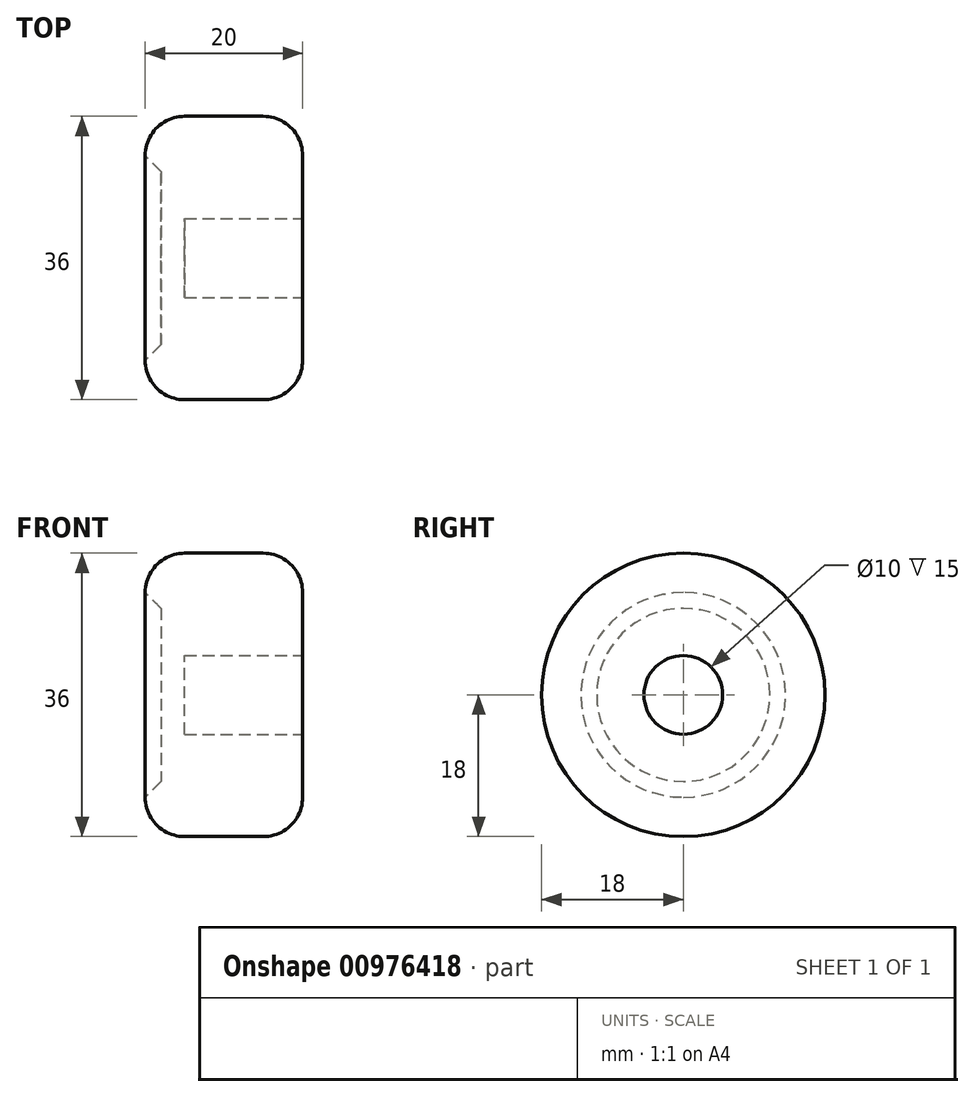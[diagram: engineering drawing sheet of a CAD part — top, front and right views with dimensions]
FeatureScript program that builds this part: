
annotation { "Feature Type Name" : "Feature", "Feature Type Description" : "" }
export const myFeature = defineFeature(function(context is Context, id is Id, definition is map)
    precondition{}
    {
        {
            var Q0;
            Q0=qCreatedBy(makeId("Right.planeOp"),FACE);
            var sketch = newSketch(context, id + "F0", { "sketchPlane" : qUnion([Q0])});
            skCircle(sketch, "E0", {"center": v(0, 0) * mm, "radius": 18 * mm});
            skSolve(sketch);
        }
        {
            var Q0;
            Q0 = qSketchRegion(id + "F0", true);
            extrude(context, id + "F1", {"entities" : qUnion([Q0]), "depth" : 20 * mm, "offsetDistance" : 25 * mm});
        }
        {
            var Q0;
            Q0=makeQuery(id+"F1.opExtrude","CAP_FACE",FACE,{"disambiguationData":[OSD([sQuery(id+"F0.wireOp",EDGE,"E0")])],"isStart":false});
            var sketch = newSketch(context, id + "F2", { "sketchPlane" : qUnion([Q0])});
            skCircle(sketch, "E1", {"center": v(0, 0) * mm, "radius": 5 * mm});
            skSolve(sketch);
        }
        {
            var Q0;
            Q0 = qSketchRegion(id + "F2", true);
            extrude(context, id + "F3", {"entities" : qUnion([Q0]), "operationType" : NewBodyOperationType.REMOVE, "oppositeDirection" : true, "depth" : 15 * mm, "offsetDistance" : 25 * mm});
        }
        {
            var Q0;
            Q0=makeQuery(id+"F1.opExtrude","CAP_EDGE",EDGE,{"disambiguationData":[OSD([sQuery(id+"F0.wireOp",EDGE,"E0")])],"isStart":true});
            var Q1;
            Q1=makeQuery(id+"F1.opExtrude","CAP_EDGE",EDGE,{"disambiguationData":[OSD([sQuery(id+"F0.wireOp",EDGE,"E0")])],"isStart":false});
            fillet(context, id + "F4", {"entities" : qUnion([Q0, Q1]), "radius" : 5 * mm, "tangentPropagation" : true, "allowEdgeOverflow" : false});
        }
        {
            var Q0;
            Q0=makeQuery(id+"F1.opExtrude","CAP_FACE",FACE,{"disambiguationData":[OSD([sQuery(id+"F0.wireOp",EDGE,"E0")])],"isStart":true});
            var sketch = newSketch(context, id + "F5", { "sketchPlane" : qUnion([Q0])});
            skCircle(sketch, "E2.0", {"center": v(0, 0) * mm, "radius": 13 * mm});
            skSolve(sketch);
        }
        {
            var Q0;
            Q0 = qSketchRegion(id + "F5", true);
            extrude(context, id + "F6", {"entities" : qUnion([Q0]), "operationType" : NewBodyOperationType.REMOVE, "oppositeDirection" : true, "depth" : 2 * mm, "offsetDistance" : 25 * mm});
        }
        {
            var Q0;
            Q0=makeQuery(id+"F6.boolean.opBoolean","COPY",EDGE,{"derivedFrom":makeQuery(id+"F6.opExtrude","CAP_EDGE",EDGE,{"disambiguationData":[OSD([sQuery(id+"F5.wireOp",EDGE,"E2.0")])],"isStart":false})});
            chamfer(context, id + "F7", {"entities" : qUnion([Q0]), "width" : 2 * mm, "tangentPropagation" : true});
        }
    });
